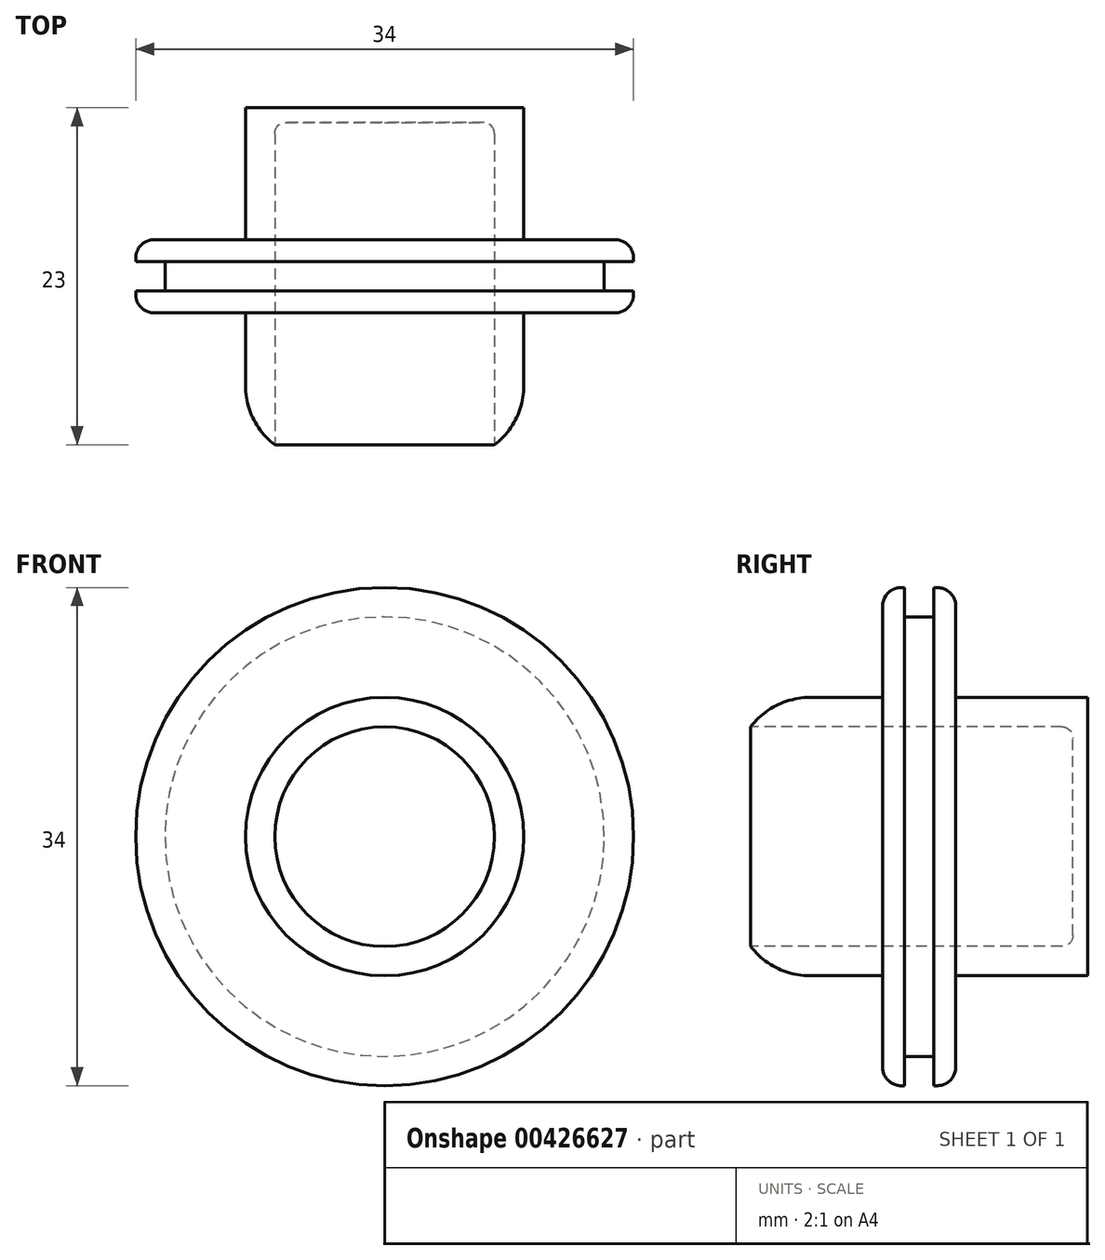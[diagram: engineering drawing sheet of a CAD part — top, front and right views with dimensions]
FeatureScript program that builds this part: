
annotation { "Feature Type Name" : "Feature", "Feature Type Description" : "" }
export const myFeature = defineFeature(function(context is Context, id is Id, definition is map)
    precondition{}
    {
        {
            var Q0;
            Q0=qCreatedBy(makeId("Front.planeOp"),FACE);
            var sketch = newSketch(context, id + "F0", { "sketchPlane" : qUnion([Q0])});
            skCircle(sketch, "E0", {"center": v(0, 0) * mm, "radius": 15 * mm});
            skSolve(sketch);
        }
        {
            var Q0;
            Q0=makeQuery(id+"F0.imprint","IMPRINT",FACE,{"disambiguationData":[TD([[makeQuery(id+"F0.imprint","IMPRINT",EDGE,{"derivedFrom":sQuery(id+"F0.wireOp",EDGE,"E0")}),1.0]])]});
            extrude(context, id + "F1", {"entities" : qUnion([Q0]), "depth" : 2 * mm});
        }
        {
            var Q0;
            Q0=makeQuery(id+"F1.opExtrude","CAP_FACE",FACE,{"disambiguationData":[OSD([sQuery(id+"F0.wireOp",EDGE,"E0")])],"isStart":false});
            var sketch = newSketch(context, id + "F2", { "sketchPlane" : qUnion([Q0])});
            skCircle(sketch, "E1", {"center": v(0, 0) * mm, "radius": 17 * mm});
            skSolve(sketch);
        }
        {
            var Q0;
            Q0=makeQuery(id+"F2.imprint","IMPRINT",FACE,{"disambiguationData":[TD([[makeQuery(id+"F2.imprint","IMPRINT",EDGE,{"derivedFrom":sQuery(id+"F2.wireOp",EDGE,"E1")}),1.0]])]});
            var Q1;
            Q1=makeQuery(id+"F2.imprint","IMPRINT",FACE,{"disambiguationData":[TD([[makeQuery(id+"F2.imprint","IMPRINT",EDGE,{"derivedFrom":makeQuery(id+"F1.opExtrude","CAP_EDGE",EDGE,{"disambiguationData":[OSD([sQuery(id+"F0.wireOp",EDGE,"E0")])],"isStart":false})}),1.0]])]});
            extrude(context, id + "F3", {"entities" : qUnion([Q0, Q1]), "operationType" : NewBodyOperationType.ADD, "depth" : 1.5 * mm});
        }
        {
            var Q0;
            Q0=makeQuery(id+"F1.opExtrude","CAP_FACE",FACE,{"disambiguationData":[OSD([sQuery(id+"F0.wireOp",EDGE,"E0")])],"isStart":true});
            var sketch = newSketch(context, id + "F4", { "sketchPlane" : qUnion([Q0])});
            skCircle(sketch, "E2", {"center": v(0, 0) * mm, "radius": 17 * mm});
            skSolve(sketch);
        }
        {
            var Q0;
            Q0=makeQuery(id+"F4.imprint","IMPRINT",FACE,{"disambiguationData":[TD([[makeQuery(id+"F4.imprint","IMPRINT",EDGE,{"derivedFrom":sQuery(id+"F4.wireOp",EDGE,"E2")}),1.0]])]});
            var Q1;
            Q1=makeQuery(id+"F4.imprint","IMPRINT",FACE,{"disambiguationData":[TD([[makeQuery(id+"F4.imprint","IMPRINT",EDGE,{"derivedFrom":makeQuery(id+"F1.opExtrude","CAP_EDGE",EDGE,{"disambiguationData":[OSD([sQuery(id+"F0.wireOp",EDGE,"E0")])],"isStart":true})}),-1.0]])]});
            extrude(context, id + "F5", {"entities" : qUnion([Q0, Q1]), "operationType" : NewBodyOperationType.ADD, "depth" : 1.5 * mm});
        }
        {
            var Q0;
            Q0=makeQuery(id+"F3.opExtrude","CAP_EDGE",EDGE,{"disambiguationData":[OSD([sQuery(id+"F2.wireOp",EDGE,"E1")])],"isStart":false});
            var Q1;
            Q1=makeQuery(id+"F5.opExtrude","CAP_EDGE",EDGE,{"disambiguationData":[OSD([sQuery(id+"F4.wireOp",EDGE,"E2")])],"isStart":false});
            fillet(context, id + "F6", {"entities" : qUnion([Q0, Q1]), "radius" : 1.27 * mm, "tangentPropagation" : true, "allowEdgeOverflow" : false});
        }
        {
            var Q0;
            Q0=makeQuery(id+"F3.opExtrude","CAP_FACE",FACE,{"disambiguationData":[OSD([sQuery(id+"F2.wireOp",EDGE,"E1")])],"isStart":false});
            var sketch = newSketch(context, id + "F7", { "sketchPlane" : qUnion([Q0])});
            skCircle(sketch, "E3", {"center": v(0, 0) * mm, "radius": 9.5 * mm});
            skSolve(sketch);
        }
        {
            var Q0;
            Q0=makeQuery(id+"F7.imprint","IMPRINT",FACE,{"disambiguationData":[TD([[makeQuery(id+"F7.imprint","IMPRINT",EDGE,{"derivedFrom":sQuery(id+"F7.wireOp",EDGE,"E3")}),1.0]])]});
            extrude(context, id + "F8", {"entities" : qUnion([Q0]), "operationType" : NewBodyOperationType.ADD, "depth" : 9 * mm});
        }
        {
            var Q0;
            Q0=makeQuery(id+"F5.opExtrude","CAP_FACE",FACE,{"disambiguationData":[OSD([sQuery(id+"F4.wireOp",EDGE,"E2")])],"isStart":false});
            var sketch = newSketch(context, id + "F9", { "sketchPlane" : qUnion([Q0])});
            skCircle(sketch, "E4", {"center": v(0, 0) * mm, "radius": 9.5 * mm});
            skSolve(sketch);
        }
        {
            var Q0;
            Q0=makeQuery(id+"F9.imprint","IMPRINT",FACE,{"disambiguationData":[TD([[makeQuery(id+"F9.imprint","IMPRINT",EDGE,{"derivedFrom":sQuery(id+"F9.wireOp",EDGE,"E4")}),1.0]])]});
            extrude(context, id + "F10", {"entities" : qUnion([Q0]), "operationType" : NewBodyOperationType.ADD, "depth" : 9 * mm});
        }
        {
            var Q0;
            Q0=makeQuery(id+"F8.opExtrude","CAP_FACE",FACE,{"disambiguationData":[OSD([sQuery(id+"F7.wireOp",EDGE,"E3")])],"isStart":false});
            var sketch = newSketch(context, id + "F11", { "sketchPlane" : qUnion([Q0])});
            skCircle(sketch, "E5", {"center": v(0, 0) * mm, "radius": 7.5 * mm});
            skSolve(sketch);
        }
        {
            var Q0;
            Q0=makeQuery(id+"F11.imprint","IMPRINT",FACE,{"disambiguationData":[TD([[makeQuery(id+"F11.imprint","IMPRINT",EDGE,{"derivedFrom":sQuery(id+"F11.wireOp",EDGE,"E5")}),1.0]])]});
            extrude(context, id + "F12", {"entities" : qUnion([Q0]), "operationType" : NewBodyOperationType.REMOVE, "oppositeDirection" : true, "depth" : 22 * mm});
        }
        {
            var Q0;
            Q0=makeQuery(id+"F12.boolean.opBoolean","COPY",FACE,{"derivedFrom":makeQuery(id+"F12.opExtrude","CAP_FACE",FACE,{"disambiguationData":[OSD([sQuery(id+"F11.wireOp",EDGE,"E5")])],"isStart":false})});
            fillet(context, id + "F13", {"entities" : qUnion([Q0]), "radius" : 0.76 * mm, "tangentPropagation" : true, "allowEdgeOverflow" : false});
        }
        {
            var Q0;
            Q0=makeQuery(id+"F8.opExtrude","CAP_EDGE",EDGE,{"disambiguationData":[OSD([sQuery(id+"F7.wireOp",EDGE,"E3")])],"isStart":false});
            fillet(context, id + "F14", {"entities" : qUnion([Q0]), "radius" : 5.08 * mm, "tangentPropagation" : true, "allowEdgeOverflow" : false});
        }
    });
